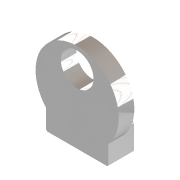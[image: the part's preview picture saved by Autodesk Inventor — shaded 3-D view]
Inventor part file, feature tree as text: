
AUTODESK INVENTOR PART (.ipt)
format: ipt  version: 2021 (Build 250183000, 183)  size: 122,880 bytes
history: native  units: in
note: dims shown in document units (in); Inventor stores cm internally (conversion verified against a paired STEP export)
features: extrude x2, sketch x2
ambient origin geometry x8: Origin, YZ Plane, XZ Plane, XY Plane, X Axis, Y Axis, Z Axis, Center Point
bodies: Solid1 (feature_tree)
feature tree (4):
  extrude  "Extrusion1"  Depth=1.6535in
  extrude  "Extrusion2"  Depth=0.5118in
  sketch  "Sketch1"  dims[d0=4.2126in d3=1.6535in]
  sketch  "Sketch2"  dims[d4=1.0827in d5=2.4016in d7=3.1496in d8=0.0787in d9=0.7874in d10=0.0in d11=3.1496in d12=1.3189in d13=0.0787in d14=0.5118in d15=0.0in]
